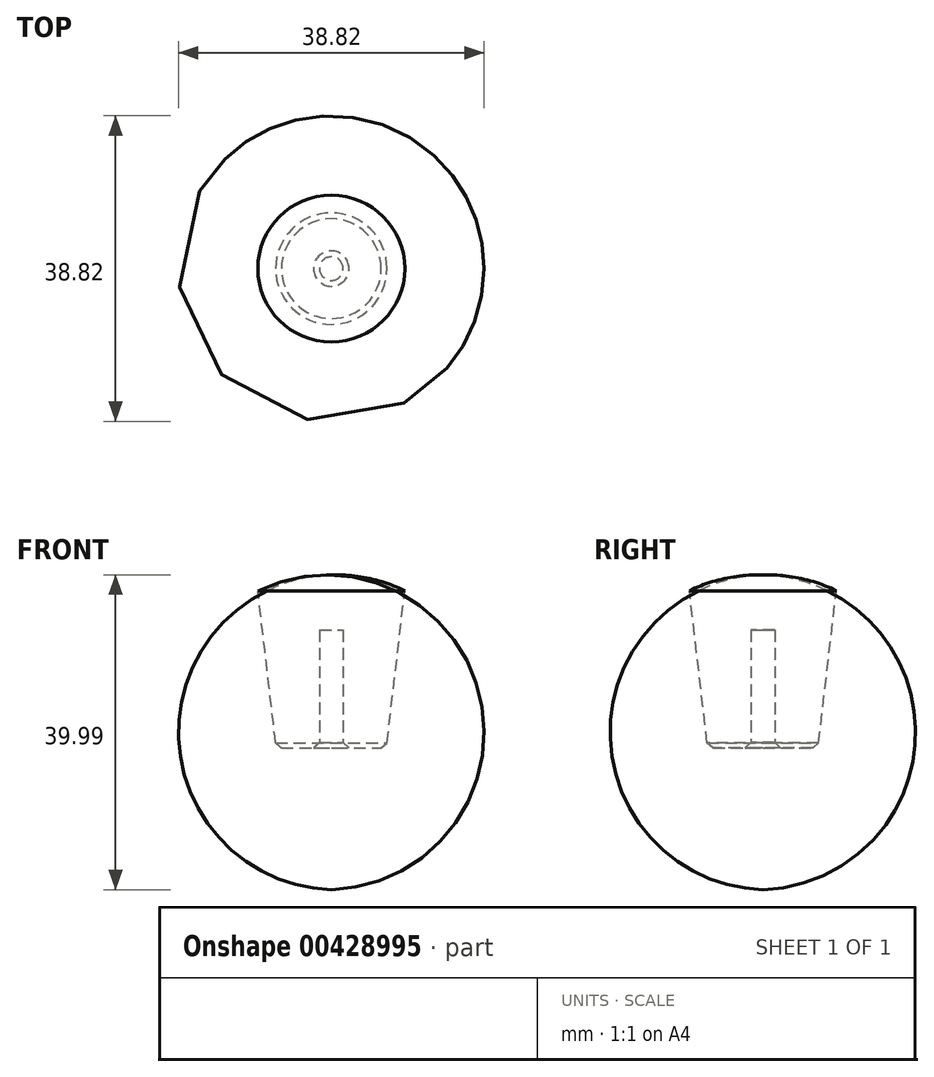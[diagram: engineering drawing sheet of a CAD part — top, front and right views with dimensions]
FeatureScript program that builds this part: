
annotation { "Feature Type Name" : "Feature", "Feature Type Description" : "" }
export const myFeature = defineFeature(function(context is Context, id is Id, definition is map)
    precondition{}
    {
        {
            var Q0;
            Q0=qCreatedBy(makeId("Front.planeOp"),FACE);
            var sketch = newSketch(context, id + "F0", { "sketchPlane" : qUnion([Q0])});
            skLineSegment(sketch, "E0", {"start": v(0, 0) * mm, "end": v(0, 34.31) * mm, "construction": true});
            skLineSegment(sketch, "E1", {"start": v(0, 15) * mm, "end": v(1.5, 15) * mm});
            skLineSegment(sketch, "E2", {"start": v(1.5, 15) * mm, "end": v(1.5, 0) * mm});
            skLineSegment(sketch, "E3", {"start": v(1.5, 0) * mm, "end": v(7, 0) * mm});
            skLineSegment(sketch, "E4", {"start": v(7, 0) * mm, "end": v(9.33, 20) * mm});
            skLineSegment(sketch, "E5", {"start": v(0, 22) * mm, "end": v(0, 15) * mm});
            skArc(sketch, "E6", {"start": v(9.33, 20) * mm, "mid": v(4.79, 21.56) * mm, "end": v(0, 22) * mm});
            skSolve(sketch);
        }
        {
            var Q0;
            Q0=makeQuery(id+"F0.imprint","IMPRINT",FACE,{"disambiguationData":[TD([[makeQuery(id+"F0.imprint","IMPRINT",EDGE,{"derivedFrom":sQuery(id+"F0.wireOp",EDGE,"E1")}),1.0]])]});
            var Q1;
            Q1=sQuery(id+"F0.wireOp",EDGE,"E0");
            revolve(context, id + "F1", {"entities" : qUnion([Q0]), "axis" : qUnion([Q1]), "revolveType" : RevolveType.FULL});
        }
        {
            var Q0;
            Q0=makeQuery(id+"F1.opRevolve","SWEPT_EDGE",EDGE,{"disambiguationData":[OSD([sQuery(id+"F0.wireOp",EDGE,"E2"),sQuery(id+"F0.wireOp",EDGE,"E3")])]});
            var Q1;
            Q1=makeQuery(id+"F1.opRevolve","SWEPT_FACE",FACE,{"disambiguationData":[OSD([sQuery(id+"F0.wireOp",EDGE,"E3")])]});
            chamfer(context, id + "F2", {"entities" : qUnion([Q0, Q1]), "width" : 0.75 * mm, "tangentPropagation" : true});
        }
    });
